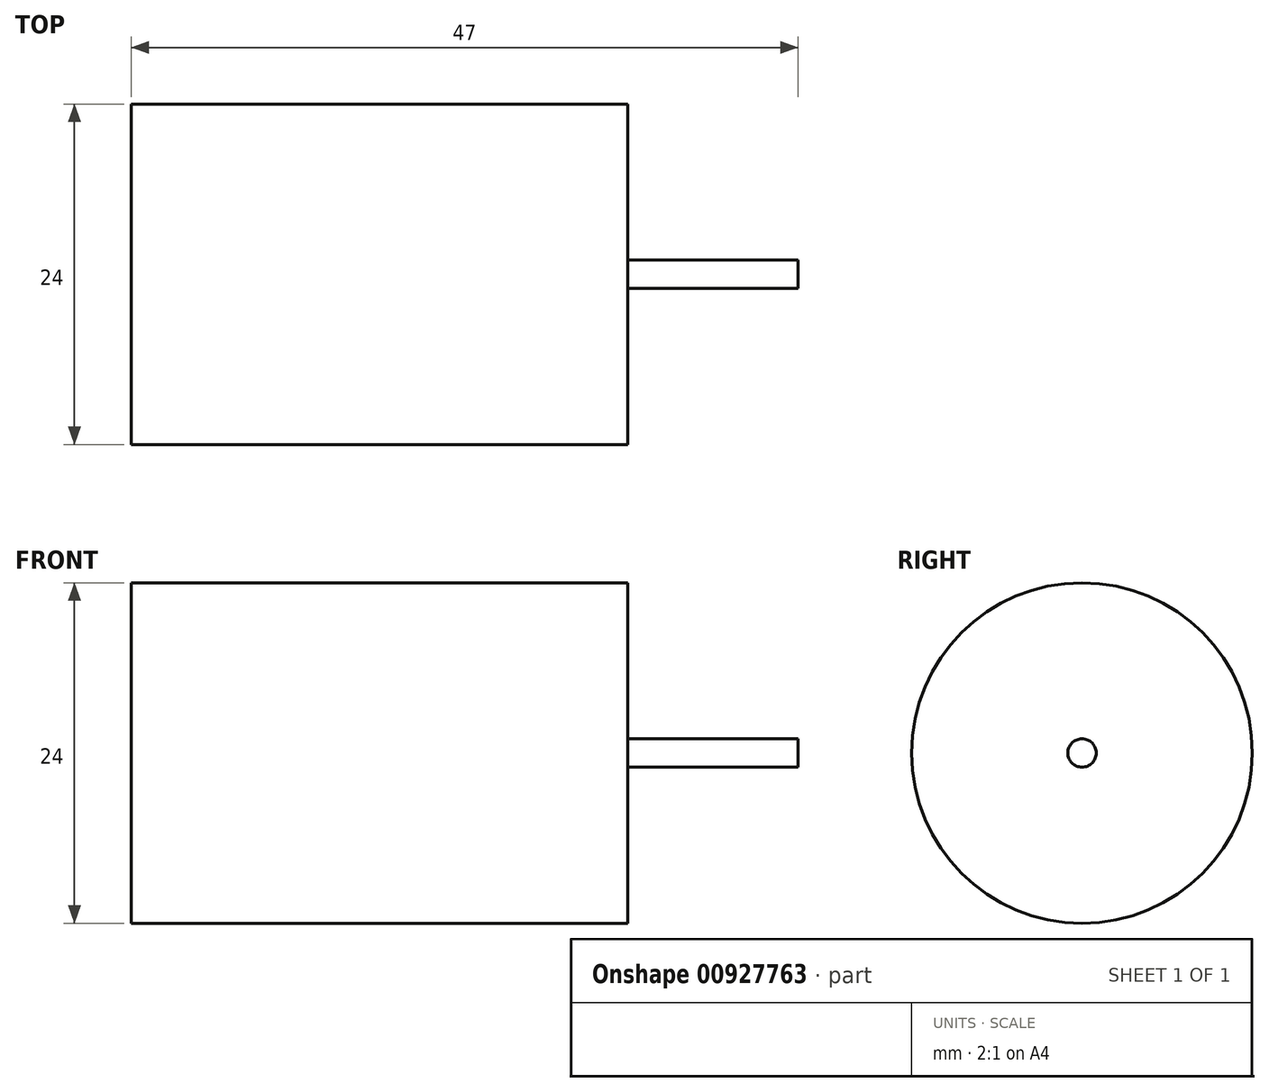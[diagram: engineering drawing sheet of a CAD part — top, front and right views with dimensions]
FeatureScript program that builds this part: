
annotation { "Feature Type Name" : "Feature", "Feature Type Description" : "" }
export const myFeature = defineFeature(function(context is Context, id is Id, definition is map)
    precondition{}
    {
        {
            var Q0;
            Q0=qCreatedBy(makeId("Right.planeOp"),FACE);
            var sketch = newSketch(context, id + "F0", { "sketchPlane" : qUnion([Q0])});
            skCircle(sketch, "E0", {"center": v(0, 0) * mm, "radius": 12 * mm});
            skSolve(sketch);
        }
        {
            var Q0;
            Q0=makeQuery(id+"F0.imprint","IMPRINT",FACE,{"disambiguationData":[TD([[makeQuery(id+"F0.imprint","IMPRINT",EDGE,{"derivedFrom":sQuery(id+"F0.wireOp",EDGE,"E0")}),1.0]])]});
            extrude(context, id + "F1", {"entities" : qUnion([Q0]), "endBound" : BoundingType.SYMMETRIC, "depth" : 35 * mm, "offsetDistance" : 25 * mm});
        }
        {
            var Q0;
            Q0=makeQuery(id+"F1.opExtrude","CAP_FACE",FACE,{"disambiguationData":[OSD([sQuery(id+"F0.wireOp",EDGE,"E0")])],"isStart":false});
            var sketch = newSketch(context, id + "F2", { "sketchPlane" : qUnion([Q0])});
            skCircle(sketch, "E1", {"center": v(0, 0) * mm, "radius": 1 * mm});
            skSolve(sketch);
        }
        {
            var Q0;
            Q0=makeQuery(id+"F2.imprint","IMPRINT",FACE,{"disambiguationData":[TD([[makeQuery(id+"F2.imprint","IMPRINT",EDGE,{"derivedFrom":sQuery(id+"F2.wireOp",EDGE,"E1")}),1.0]])]});
            extrude(context, id + "F3", {"entities" : qUnion([Q0]), "depth" : 12 * mm, "offsetDistance" : 25 * mm});
        }
    });
